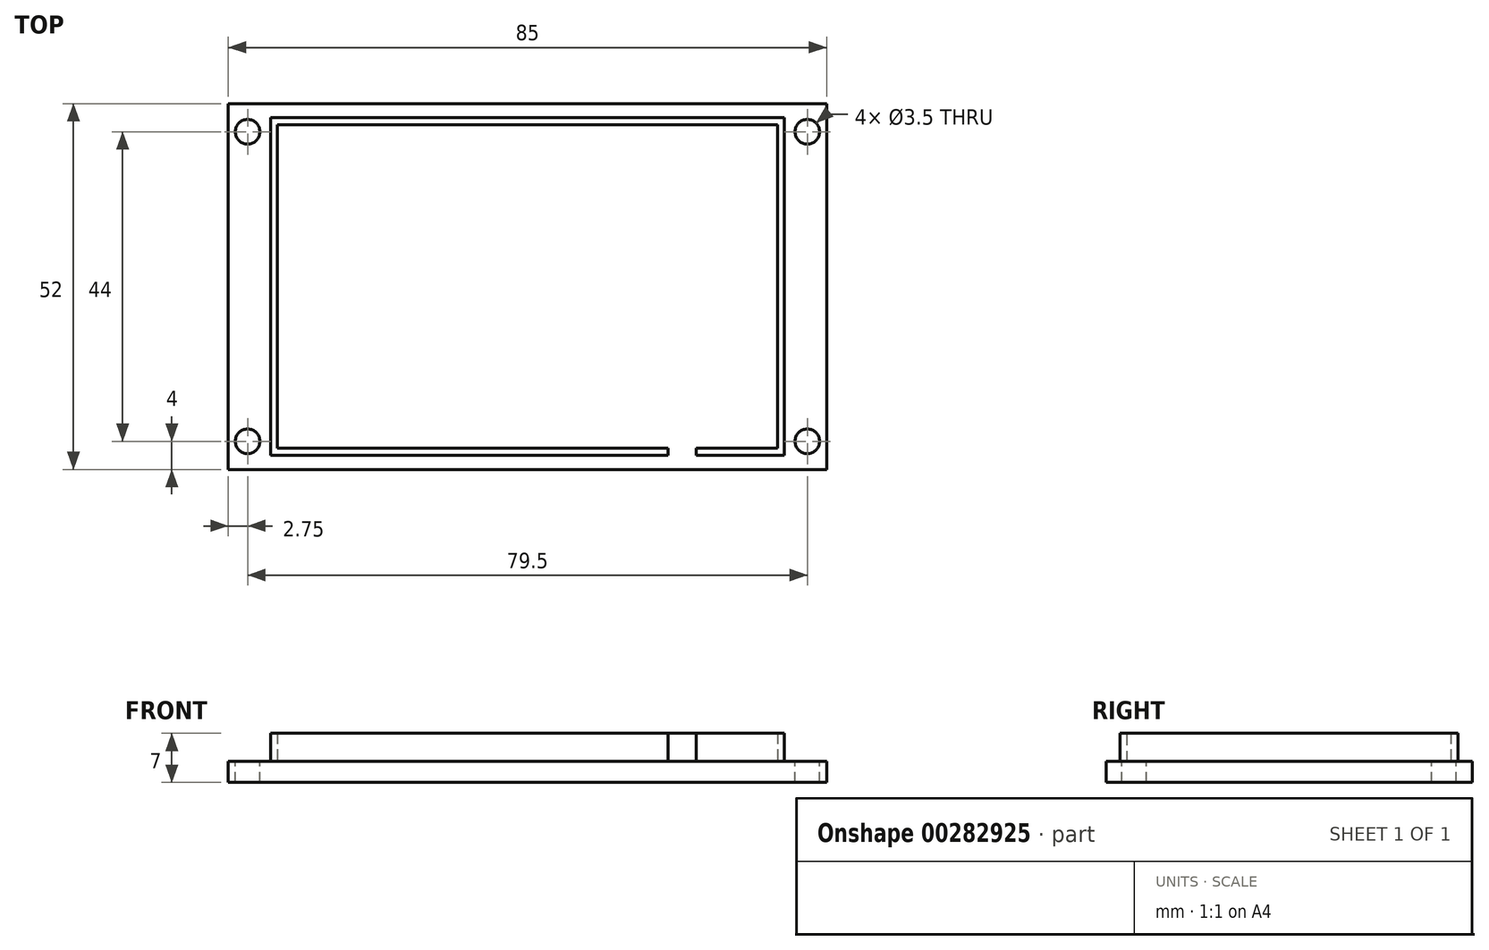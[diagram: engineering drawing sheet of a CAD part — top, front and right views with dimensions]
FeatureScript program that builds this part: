
annotation { "Feature Type Name" : "Feature", "Feature Type Description" : "" }
export const myFeature = defineFeature(function(context is Context, id is Id, definition is map)
    precondition{}
    {
        {
            var Q0;
            Q0=qCreatedBy(makeId("Top.planeOp"),FACE);
            var sketch = newSketch(context, id + "F0", { "sketchPlane" : qUnion([Q0])});
            skLineSegment(sketch, "E0.bottom", {"start": v(-42.5, 26) * mm, "end": v(42.5, 26) * mm});
            skLineSegment(sketch, "E0.top", {"start": v(-42.5, -26) * mm, "end": v(42.5, -26) * mm});
            skLineSegment(sketch, "E0.left", {"start": v(-42.5, 26) * mm, "end": v(-42.5, -26) * mm});
            skLineSegment(sketch, "E0.right", {"start": v(42.5, 26) * mm, "end": v(42.5, -26) * mm});
            skPoint(sketch, "E0.middle", {"position": v(0, 0) * mm});
            skSolve(sketch);
        }
        {
            var Q0;
            Q0 = qSketchRegion(id + "F0", true);
            extrude(context, id + "F1", {"entities" : qUnion([Q0]), "depth" : 3 * mm});
        }
        {
            var Q0;
            Q0=makeQuery(id+"F1.opExtrude","CAP_FACE",FACE,{"disambiguationData":[OSD([sQuery(id+"F0.wireOp",EDGE,"E0.bottom"),sQuery(id+"F0.wireOp",EDGE,"E0.top"),sQuery(id+"F0.wireOp",EDGE,"E0.left"),sQuery(id+"F0.wireOp",EDGE,"E0.right")])],"isStart":false});
            var sketch = newSketch(context, id + "F2", { "sketchPlane" : qUnion([Q0])});
            skLineSegment(sketch, "E1", {"start": v(-42.5, 26) * mm, "end": v(-39.75, 26) * mm, "construction": true});
            skLineSegment(sketch, "E2", {"start": v(-39.75, 26) * mm, "end": v(-39.75, 22) * mm, "construction": true});
            skCircle(sketch, "E3", {"center": v(-39.75, 22) * mm, "radius": 1.75 * mm});
            skCircle(sketch, "E4.MirrorC", {"center": v(-39.75, -22) * mm, "radius": 1.75 * mm});
            skCircle(sketch, "E5.MirrorC", {"center": v(39.75, 22) * mm, "radius": 1.75 * mm});
            skCircle(sketch, "E6.MirrorC", {"center": v(39.75, -22) * mm, "radius": 1.75 * mm});
            skSolve(sketch);
        }
        {
            var Q0;
            Q0 = qSketchRegion(id + "F2", true);
            extrude(context, id + "F3", {"entities" : qUnion([Q0]), "operationType" : NewBodyOperationType.REMOVE, "oppositeDirection" : true, "depth" : 25 * mm});
        }
        {
            var Q0;
            Q0=makeQuery(id+"F1.opExtrude","CAP_FACE",FACE,{"disambiguationData":[OSD([sQuery(id+"F0.wireOp",EDGE,"E0.bottom"),sQuery(id+"F0.wireOp",EDGE,"E0.top"),sQuery(id+"F0.wireOp",EDGE,"E0.left"),sQuery(id+"F0.wireOp",EDGE,"E0.right")])],"isStart":false});
            var sketch = newSketch(context, id + "F4", { "sketchPlane" : qUnion([Q0])});
            skLineSegment(sketch, "E7.bottom", {"start": v(-36.5, 24) * mm, "end": v(36.5, 24) * mm});
            skLineSegment(sketch, "E7.top", {"start": v(-36.5, -24) * mm, "end": v(36.5, -24) * mm});
            skLineSegment(sketch, "E7.left", {"start": v(-36.5, 24) * mm, "end": v(-36.5, -24) * mm});
            skLineSegment(sketch, "E7.right", {"start": v(36.5, 24) * mm, "end": v(36.5, -24) * mm});
            skPoint(sketch, "E7.middle", {"position": v(0, 0) * mm});
            skLineSegment(sketch, "E8.bottom", {"start": v(-35.5, 23) * mm, "end": v(35.5, 23) * mm});
            skLineSegment(sketch, "E8.top", {"start": v(-35.5, -23) * mm, "end": v(35.5, -23) * mm});
            skLineSegment(sketch, "E8.left", {"start": v(-35.5, 23) * mm, "end": v(-35.5, -23) * mm});
            skLineSegment(sketch, "E8.right", {"start": v(35.5, 23) * mm, "end": v(35.5, -23) * mm});
            skSolve(sketch);
        }
        {
            var Q0;
            Q0 = qSketchRegion(id + "F4", true);
            extrude(context, id + "F5", {"entities" : qUnion([Q0]), "operationType" : NewBodyOperationType.ADD, "depth" : 4 * mm});
        }
        {
            var Q0;
            Q0=makeQuery(id+"F5.opExtrude","CAP_FACE",FACE,{"disambiguationData":[OSD([sQuery(id+"F4.wireOp",EDGE,"E7.bottom"),sQuery(id+"F4.wireOp",EDGE,"E7.top"),sQuery(id+"F4.wireOp",EDGE,"E7.left"),sQuery(id+"F4.wireOp",EDGE,"E7.right"),sQuery(id+"F4.wireOp",EDGE,"E8.bottom"),sQuery(id+"F4.wireOp",EDGE,"E8.top"),sQuery(id+"F4.wireOp",EDGE,"E8.left"),sQuery(id+"F4.wireOp",EDGE,"E8.right")])],"isStart":false});
            var sketch = newSketch(context, id + "F6", { "sketchPlane" : qUnion([Q0])});
            skLineSegment(sketch, "E9", {"start": v(0, -24) * mm, "end": v(20, -24) * mm, "construction": true});
            skLineSegment(sketch, "E10", {"start": v(20, -24) * mm, "end": v(20, -23) * mm});
            skLineSegment(sketch, "E11", {"start": v(20, -23) * mm, "end": v(24, -23) * mm});
            skLineSegment(sketch, "E12", {"start": v(24, -23) * mm, "end": v(24, -24) * mm});
            skLineSegment(sketch, "E13", {"start": v(24, -24) * mm, "end": v(20, -24) * mm});
            skSolve(sketch);
        }
        {
            var Q0;
            Q0 = qSketchRegion(id + "F6", true);
            extrude(context, id + "F7", {"entities" : qUnion([Q0]), "operationType" : NewBodyOperationType.REMOVE, "oppositeDirection" : true, "depth" : 4 * mm});
        }
    });
